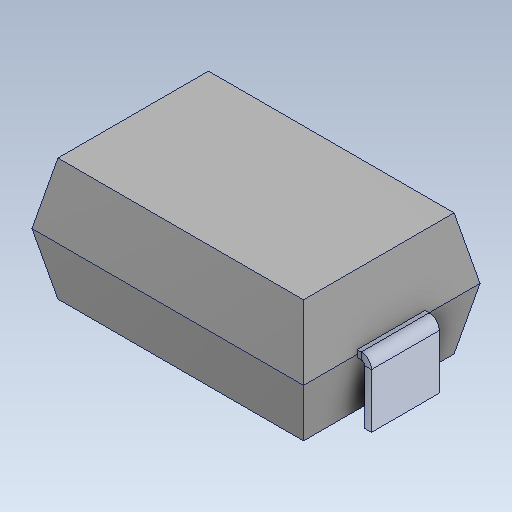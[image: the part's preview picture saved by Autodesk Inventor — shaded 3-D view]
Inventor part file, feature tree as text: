
AUTODESK INVENTOR PART (.ipt)
format: ipt  version: 2020 (Build 240168000, 168)  size: 114,176 bytes
history: native  units: in
note: dims shown in document units (in); Inventor stores cm internally (conversion verified against a paired STEP export)
features: mirror x1
ambient origin geometry x8: Origin, YZ Plane, XZ Plane, XY Plane, X Axis, Y Axis, Z Axis, Center Point
bodies: Solid1 (feature_tree)
feature tree (1):
  mirror  "Mirror2"
